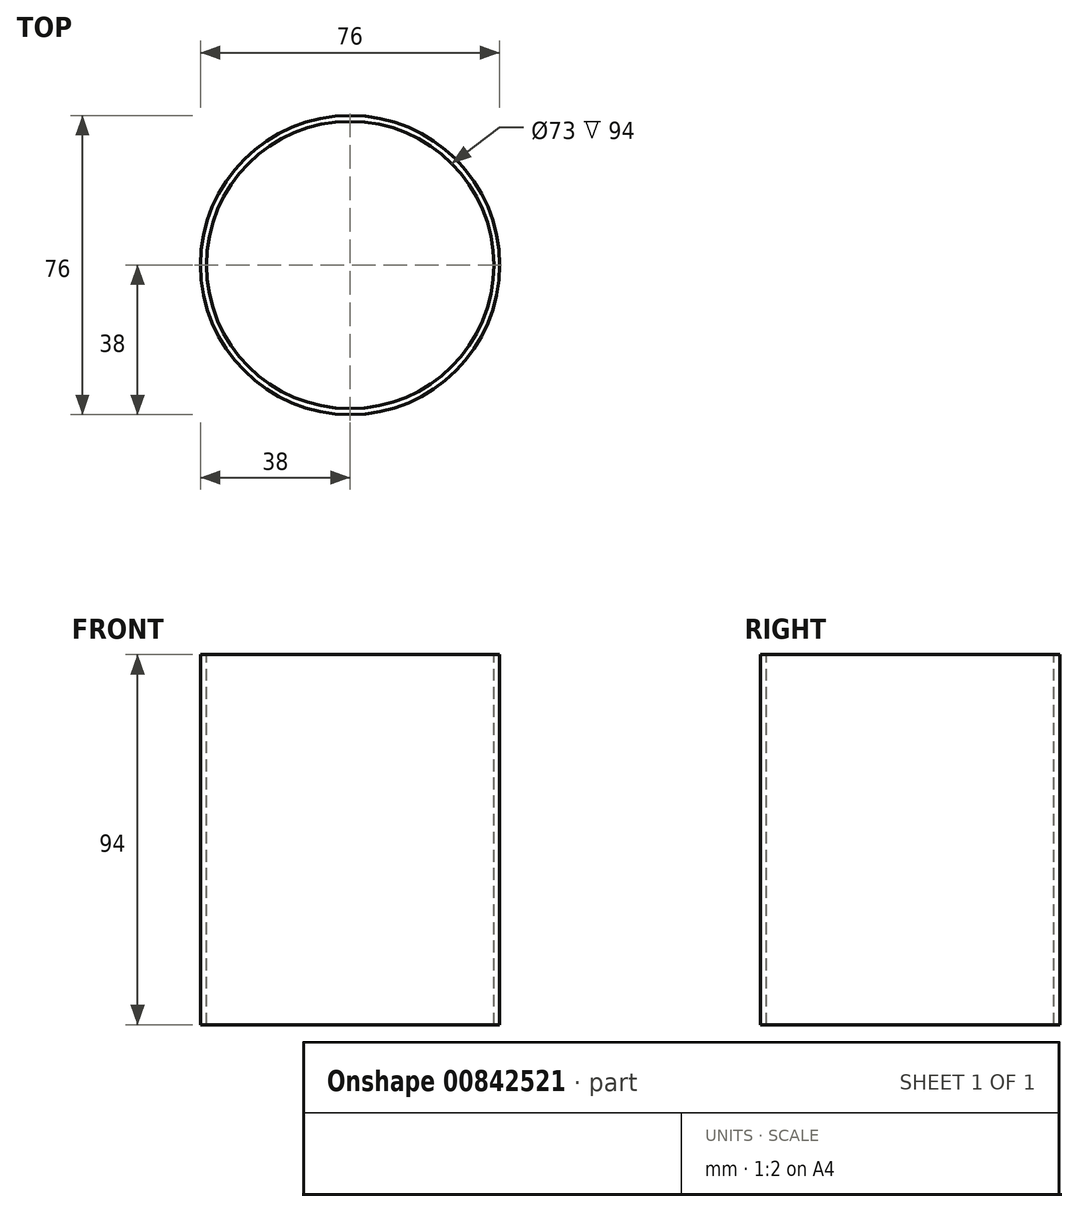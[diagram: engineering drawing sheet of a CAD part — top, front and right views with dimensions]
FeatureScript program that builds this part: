
annotation { "Feature Type Name" : "Feature", "Feature Type Description" : "" }
export const myFeature = defineFeature(function(context is Context, id is Id, definition is map)
    precondition{}
    {
        {
            var Q0;
            Q0=qCreatedBy(makeId("Top.planeOp"),FACE);
            var sketch = newSketch(context, id + "F0", { "sketchPlane" : qUnion([Q0])});
            skCircle(sketch, "E0", {"center": v(0, 0) * mm, "radius": 38 * mm});
            skCircle(sketch, "E1", {"center": v(0, 0) * mm, "radius": 36.5 * mm});
            skSolve(sketch);
        }
        {
            var Q0;
            Q0 = qSketchRegion(id + "F0", true);
            extrude(context, id + "F1", {"entities" : qUnion([Q0]), "oppositeDirection" : true, "depth" : 94 * mm, "offsetDistance" : 25 * mm});
        }
    });
